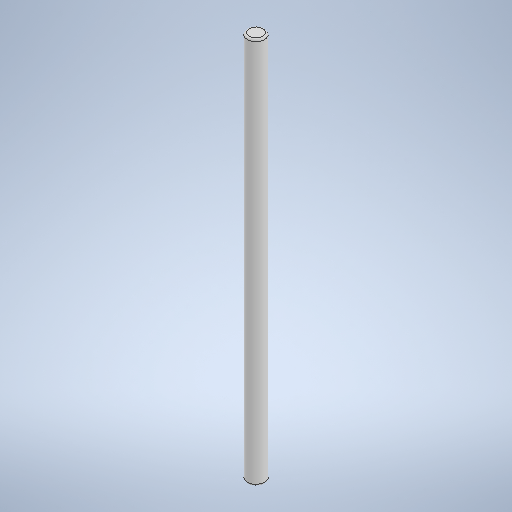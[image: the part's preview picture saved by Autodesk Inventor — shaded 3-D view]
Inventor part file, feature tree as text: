
AUTODESK INVENTOR PART (.ipt)
format: ipt  version: 2025 (Build 290162000, 162)  size: 250,368 bytes
history: native  units: in
note: dims shown in document units (in); Inventor stores cm internally (conversion verified against a paired STEP export)
features: extrude x1, fillet x1, sketch x1
ambient origin geometry x8: Origin, YZ Plane, XZ Plane, XY Plane, X Axis, Y Axis, Z Axis, Center Point
bodies: Solid1 (feature_tree)
feature tree (3):
  extrude  "Extrusion1"  Depth=15.748in TaperAngle=0.0deg
  fillet  "Fillet1"  Radius=0.0787in
  sketch  "Sketch1"  dims[d0=0.7047in d1=15.748in d2=0.0in d3=0.0787in]
